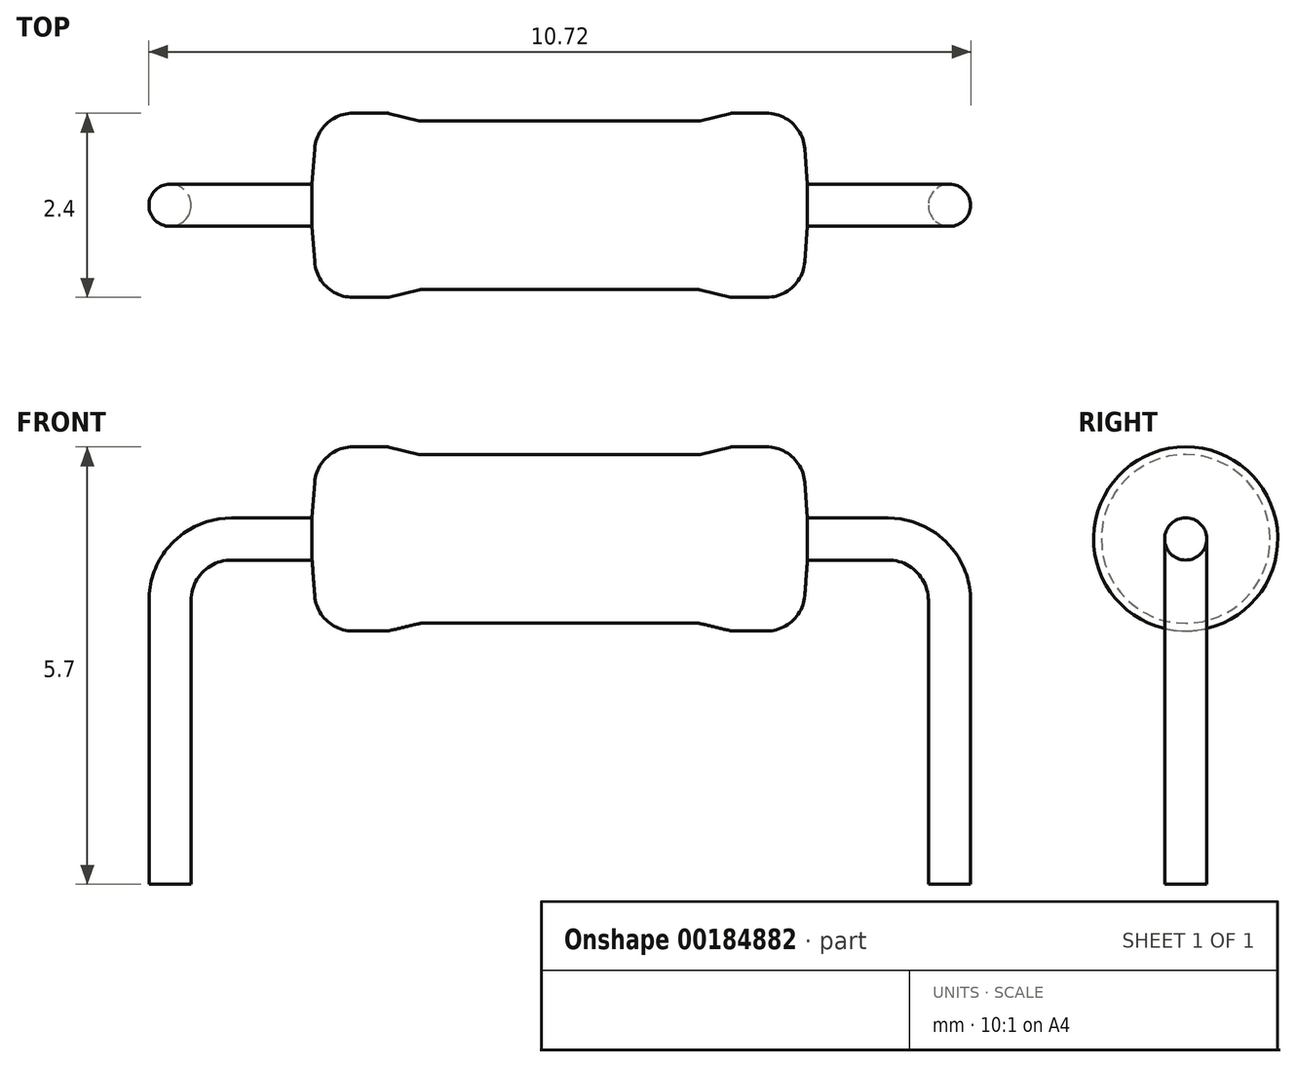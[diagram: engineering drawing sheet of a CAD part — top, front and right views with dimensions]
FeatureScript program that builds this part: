
annotation { "Feature Type Name" : "Feature", "Feature Type Description" : "" }
export const myFeature = defineFeature(function(context is Context, id is Id, definition is map)
    precondition{}
    {
        {
            var Q0;
            Q0=qCreatedBy(makeId("Top.planeOp"),FACE);
            var sketch = newSketch(context, id + "F0", { "sketchPlane" : qUnion([Q0])});
            skLineSegment(sketch, "E0", {"start": v(-3.25, 0) * mm, "end": v(-3.2, 0.74) * mm});
            skLineSegment(sketch, "E1", {"start": v(-2.7, 1.2) * mm, "end": v(-2.25, 1.2) * mm});
            skLineSegment(sketch, "E2", {"start": v(-2.23, 1.2) * mm, "end": v(-1.83, 1.1) * mm});
            skLineSegment(sketch, "E3", {"start": v(-1.8, 1.1) * mm, "end": v(0, 1.1) * mm});
            skLineSegment(sketch, "E4", {"start": v(0, 1.1) * mm, "end": v(0, 0) * mm});
            skLineSegment(sketch, "E5", {"start": v(0, 0) * mm, "end": v(-3.25, 0) * mm});
            skPoint(sketch, "E6.visualSharp", {"position": v(-3.16, 1.2) * mm});
            skArc(sketch, "E6.filletArc", {"start": v(-2.7, 1.2) * mm, "mid": v(-3.04, 1.07) * mm, "end": v(-3.2, 0.74) * mm});
            skPoint(sketch, "E7.visualSharp", {"position": v(-2.24, 1.2) * mm});
            skArc(sketch, "E7.filletArc", {"start": v(-2.23, 1.2) * mm, "mid": v(-2.24, 1.2) * mm, "end": v(-2.25, 1.2) * mm});
            skPoint(sketch, "E8.visualSharp", {"position": v(-1.82, 1.1) * mm});
            skArc(sketch, "E8.filletArc", {"start": v(-1.83, 1.1) * mm, "mid": v(-1.82, 1.1) * mm, "end": v(-1.8, 1.1) * mm});
            skSolve(sketch);
        }
        {
            var Q0;
            Q0=qSketchRegion(id+"F0",true);
            var Q1;
            Q1=sQuery(id+"F0.wireOp",EDGE,"E5");
            revolve(context, id + "F1", {"entities" : qUnion([Q0]), "axis" : qUnion([Q1]), "revolveType" : RevolveType.FULL});
        }
        {
            var Q0;
            Q0=makeQuery(id+"F1.opRevolve","SWEPT_BODY",BODY,{"disambiguationData":[OSD([sQuery(id+"F0.wireOp",EDGE,"E0"),sQuery(id+"F0.wireOp",EDGE,"E1"),sQuery(id+"F0.wireOp",EDGE,"E2"),sQuery(id+"F0.wireOp",EDGE,"E3"),sQuery(id+"F0.wireOp",EDGE,"E4"),sQuery(id+"F0.wireOp",EDGE,"E5"),sQuery(id+"F0.wireOp",EDGE,"E6.filletArc"),sQuery(id+"F0.wireOp",EDGE,"E7.filletArc"),sQuery(id+"F0.wireOp",EDGE,"E8.filletArc")])]});
            var Q1;
            Q1=makeQuery(id+"F1.opRevolve","SWEPT_FACE",FACE,{"disambiguationData":[OSD([sQuery(id+"F0.wireOp",EDGE,"E4")])]});
            mirror(context, id + "F2", {"operationType" : NewBodyOperationType.ADD, "entities" : qUnion([Q0]), "mirrorPlane" : qUnion([Q1])});
        }
        {
            var Q0;
            Q0=qCreatedBy(makeId("Right.planeOp"),FACE);
            var sketch = newSketch(context, id + "F3", { "sketchPlane" : qUnion([Q0])});
            skCircle(sketch, "E9", {"center": v(0, 0) * mm, "radius": 0.28 * mm});
            skSolve(sketch);
        }
        {
            var Q0;
            Q0=qCreatedBy(makeId("Front.planeOp"),FACE);
            var sketch = newSketch(context, id + "F4", { "sketchPlane" : qUnion([Q0])});
            skLineSegment(sketch, "E10", {"start": v(0, 0) * mm, "end": v(4.28, 0) * mm});
            skLineSegment(sketch, "E11", {"start": v(5.08, -0.8) * mm, "end": v(5.08, -4.5) * mm});
            skPoint(sketch, "E12.visualSharp", {"position": v(5.08, 0) * mm});
            skArc(sketch, "E12.filletArc", {"start": v(5.08, -0.8) * mm, "mid": v(4.85, -0.23) * mm, "end": v(4.28, 0) * mm});
            skSolve(sketch);
        }
        {
            var Q0;
            Q0=qSketchRegion(id+"F3",true);
            var Q1;
            Q1=qConstructionFilter(qBodyType(qCreatedBy(id+"F4",EDGE),BodyType.WIRE),ConstructionObject.NO);
            sweep(context, id + "F5", {"profiles" : qUnion([Q0]), "path" : qUnion([Q1])});
        }
        {
            var Q0;
            Q0=makeQuery(id+"F5.opSweep","SWEPT_BODY",BODY,{"disambiguationData":[OSD([sQuery(id+"F3.wireOp",EDGE,"E9"),sQuery(id+"F4.wireOp",EDGE,"E10")])]});
            var Q1;
            Q1=qCreatedBy(makeId("Right.planeOp"),FACE);
            mirror(context, id + "F6", {"operationType" : NewBodyOperationType.ADD, "entities" : qUnion([Q0]), "mirrorPlane" : qUnion([Q1])});
        }
    });
